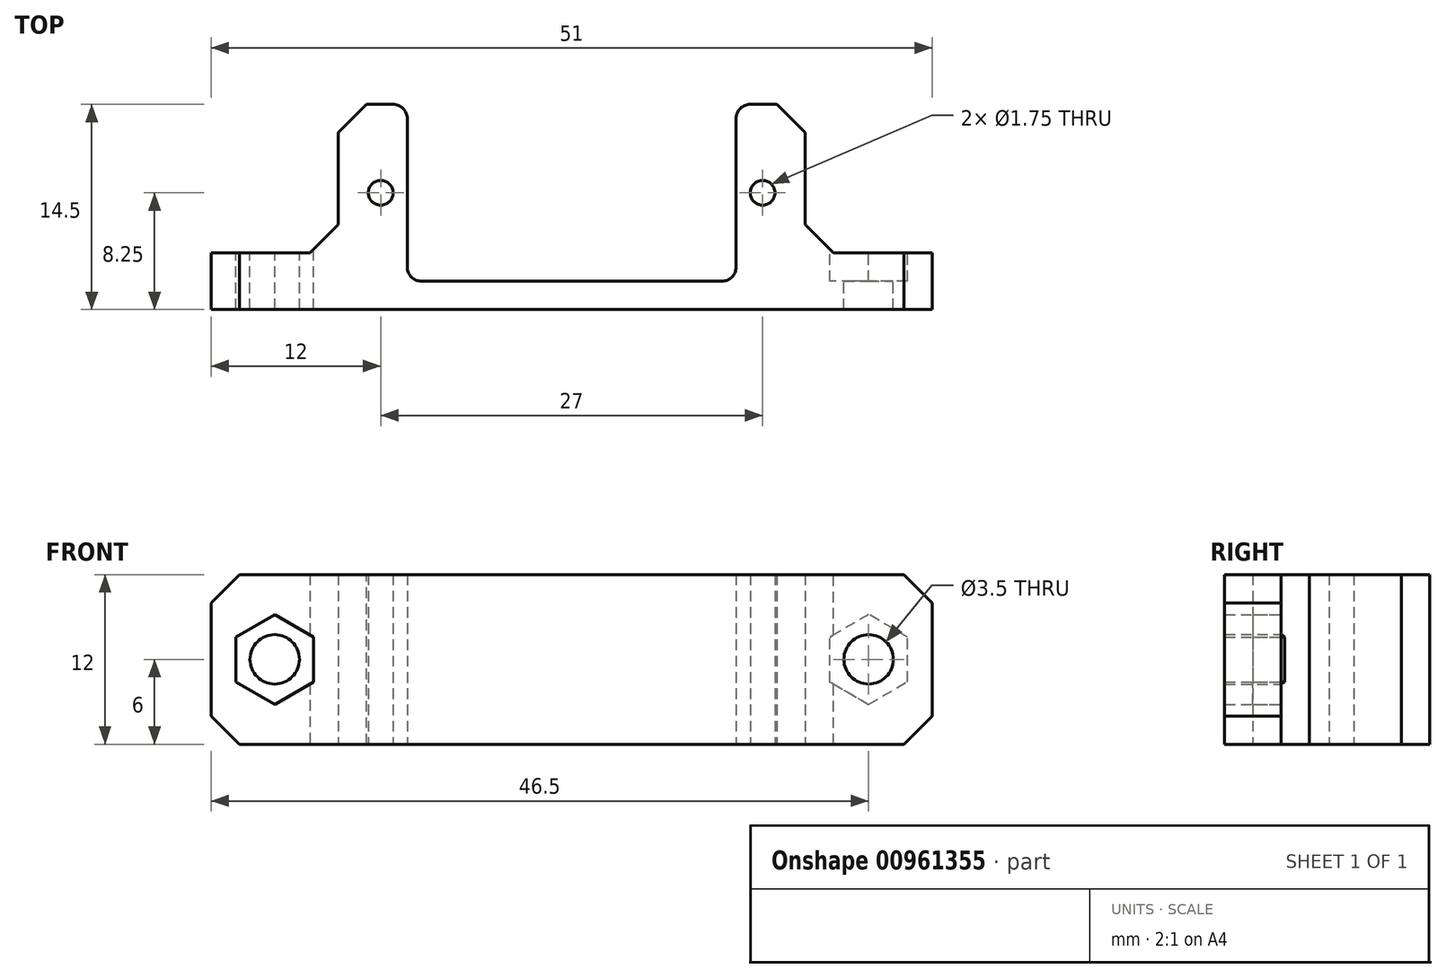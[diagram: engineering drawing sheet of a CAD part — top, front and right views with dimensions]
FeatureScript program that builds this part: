
annotation { "Feature Type Name" : "Feature", "Feature Type Description" : "" }
export const myFeature = defineFeature(function(context is Context, id is Id, definition is map)
    precondition{}
    {
        {
            var Q0;
            Q0=qCreatedBy(makeId("Top.planeOp"),FACE);
            var sketch = newSketch(context, id + "F0", { "sketchPlane" : qUnion([Q0])});
            skLineSegment(sketch, "E0.bottom", {"start": v(16.5, 7.25) * mm, "end": v(-16.5, 7.25) * mm});
            skLineSegment(sketch, "E0.top", {"start": v(16.5, -7.25) * mm, "end": v(-16.5, -7.25) * mm});
            skLineSegment(sketch, "E0.left", {"start": v(16.5, 7.25) * mm, "end": v(16.5, -7.25) * mm});
            skLineSegment(sketch, "E0.right", {"start": v(-16.5, 7.25) * mm, "end": v(-16.5, -7.25) * mm});
            skPoint(sketch, "E0.middle", {"position": v(0, 0) * mm});
            skLineSegment(sketch, "E1", {"start": v(-16.5, -5.25) * mm, "end": v(16.5, -5.25) * mm});
            skLineSegment(sketch, "E2", {"start": v(-11.62, 7.25) * mm, "end": v(-11.62, -5.25) * mm});
            skCircle(sketch, "E3", {"center": v(-13.5, 1) * mm, "radius": 0.88 * mm});
            skLineSegment(sketch, "E4.bottom", {"start": v(-25.5, -3.25) * mm, "end": v(-16.5, -3.25) * mm});
            skLineSegment(sketch, "E4.top", {"start": v(-25.5, -7.25) * mm, "end": v(-16.5, -7.25) * mm});
            skLineSegment(sketch, "E4.left", {"start": v(-25.5, -3.25) * mm, "end": v(-25.5, -7.25) * mm});
            skLineSegment(sketch, "E4.right", {"start": v(-16.5, -3.25) * mm, "end": v(-16.5, -7.25) * mm});
            skLineSegment(sketch, "E5.MirrorCS", {"start": v(11.62, 7.25) * mm, "end": v(11.62, -5.25) * mm});
            skCircle(sketch, "E6.MirrorC", {"center": v(13.5, 1) * mm, "radius": 0.88 * mm});
            skLineSegment(sketch, "E7.MirrorCS", {"start": v(25.5, -3.25) * mm, "end": v(16.5, -3.25) * mm});
            skLineSegment(sketch, "E8.MirrorCS", {"start": v(25.5, -3.25) * mm, "end": v(25.5, -7.25) * mm});
            skLineSegment(sketch, "E9.MirrorCS", {"start": v(25.5, -7.25) * mm, "end": v(16.5, -7.25) * mm});
            skSolve(sketch);
        }
        {
            var Q0;
            {var subQ4=sQuery(id+"F0.wireOp",EDGE,"E0.top");Q0=makeQuery(id+"F0.imprint","IMPRINT",FACE,{"disambiguationData":[TD([[makeQuery(id+"F0.imprint","IMPRINT",EDGE,{"derivedFrom":subQ4}),-1.0]])]});}
            var Q1;
            {var subQ4=sQuery(id+"F0.wireOp",EDGE,"E2");Q1=makeQuery(id+"F0.imprint","IMPRINT",FACE,{"disambiguationData":[TD([[makeQuery(id+"F0.imprint","IMPRINT",EDGE,{"derivedFrom":subQ4}),-1.0]])]});}
            var Q2;
            {var subQ6=sQuery(id+"F0.wireOp",EDGE,"E5.MirrorCS");Q2=makeQuery(id+"F0.imprint","IMPRINT",FACE,{"disambiguationData":[TD([[makeQuery(id+"F0.imprint","IMPRINT",EDGE,{"derivedFrom":subQ6}),1.0]])]});}
            var Q3;
            {var subQ3=sQuery(id+"F0.wireOp",EDGE,"E7.MirrorCS");Q3=makeQuery(id+"F0.imprint","IMPRINT",FACE,{"disambiguationData":[TD([[makeQuery(id+"F0.imprint","IMPRINT",EDGE,{"derivedFrom":subQ3}),1.0]])]});}
            var Q4;
            {var subQ1=sQuery(id+"F0.wireOp",EDGE,"E4.bottom");Q4=makeQuery(id+"F0.imprint","IMPRINT",FACE,{"disambiguationData":[TD([[makeQuery(id+"F0.imprint","IMPRINT",EDGE,{"derivedFrom":subQ1}),-1.0]])]});}
            extrude(context, id + "F1", {"entities" : qUnion([Q0, Q1, Q2, Q3, Q4]), "depth" : 12 * mm, "offsetDistance" : 25 * mm});
        }
        {
            var Q0;
            Q0=makeQuery(id+"F1.opExtrude","SWEPT_FACE",FACE,{"disambiguationData":[OSD([sQuery(id+"F0.wireOp",EDGE,"E7.MirrorCS")])]});
            var sketch = newSketch(context, id + "F2", { "sketchPlane" : qUnion([Q0])});
            skCircle(sketch, "E10.cCircle", {"center": v(-21, 6) * mm, "radius": 2.75 * mm, "construction": true});
            skLineSegment(sketch, "E10.0", {"start": v(-18.25, 7.59) * mm, "end": v(-18.25, 4.41) * mm});
            skLineSegment(sketch, "E10.1", {"start": v(-18.25, 4.41) * mm, "end": v(-21, 2.82) * mm});
            skLineSegment(sketch, "E10.2", {"start": v(-21, 2.82) * mm, "end": v(-23.75, 4.41) * mm});
            skLineSegment(sketch, "E10.3", {"start": v(-23.75, 4.41) * mm, "end": v(-23.75, 7.59) * mm});
            skLineSegment(sketch, "E10.4", {"start": v(-23.75, 7.59) * mm, "end": v(-21, 9.18) * mm});
            skLineSegment(sketch, "E10.5", {"start": v(-21, 9.18) * mm, "end": v(-18.25, 7.59) * mm});
            skPoint(sketch, "E10.0.midPoint", {"position": v(-18.25, 6) * mm});
            skCircle(sketch, "E11", {"center": v(-21, 6) * mm, "radius": 1.75 * mm});
            skLineSegment(sketch, "E12.MirrorCS", {"start": v(18.25, 7.59) * mm, "end": v(18.25, 4.41) * mm});
            skLineSegment(sketch, "E13.MirrorCS", {"start": v(21, 9.18) * mm, "end": v(18.25, 7.59) * mm});
            skLineSegment(sketch, "E14.MirrorCS", {"start": v(23.75, 7.59) * mm, "end": v(21, 9.18) * mm});
            skLineSegment(sketch, "E15.MirrorCS", {"start": v(23.75, 4.41) * mm, "end": v(23.75, 7.59) * mm});
            skLineSegment(sketch, "E16.MirrorCS", {"start": v(21, 2.82) * mm, "end": v(23.75, 4.41) * mm});
            skLineSegment(sketch, "E17.MirrorCS", {"start": v(18.25, 4.41) * mm, "end": v(21, 2.82) * mm});
            skCircle(sketch, "E18.MirrorC", {"center": v(21, 6) * mm, "radius": 1.75 * mm});
            skCircle(sketch, "E19.MirrorC", {"center": v(21, 6) * mm, "radius": 2.75 * mm, "construction": true});
            skPoint(sketch, "E20.MirrorP", {"position": v(18.25, 6) * mm});
            skSolve(sketch);
        }
        {
            var Q0;
            Q0=makeQuery(id+"F2.imprint","IMPRINT",FACE,{"disambiguationData":[TD([[makeQuery(id+"F2.imprint","IMPRINT",EDGE,{"derivedFrom":sQuery(id+"F2.wireOp",EDGE,"E11")}),1.0]])]});
            var Q1;
            Q1=makeQuery(id+"F2.imprint","IMPRINT",FACE,{"disambiguationData":[TD([[makeQuery(id+"F2.imprint","IMPRINT",EDGE,{"derivedFrom":sQuery(id+"F2.wireOp",EDGE,"E18.MirrorC")}),-1.0]])]});
            extrude(context, id + "F3", {"entities" : qUnion([Q0, Q1]), "operationType" : NewBodyOperationType.REMOVE, "endBound" : BoundingType.THROUGH_ALL, "oppositeDirection" : true, "depth" : 25 * mm, "offsetDistance" : 25 * mm});
        }
        {
            var Q0;
            Q0=makeQuery(id+"F2.imprint","IMPRINT",FACE,{"disambiguationData":[TD([[makeQuery(id+"F2.imprint","IMPRINT",EDGE,{"derivedFrom":sQuery(id+"F2.wireOp",EDGE,"E10.0")}),-1.0]])]});
            var Q1;
            Q1=makeQuery(id+"F2.imprint","IMPRINT",FACE,{"disambiguationData":[TD([[makeQuery(id+"F2.imprint","IMPRINT",EDGE,{"derivedFrom":sQuery(id+"F2.wireOp",EDGE,"E12.MirrorCS")}),1.0]])]});
            extrude(context, id + "F4", {"entities" : qUnion([Q0, Q1]), "operationType" : NewBodyOperationType.REMOVE, "oppositeDirection" : true, "depth" : 2 * mm, "offsetDistance" : 25 * mm});
        }
        {
            var Q0;
            Q0=makeQuery(id+"F1.opExtrude","SWEPT_EDGE",EDGE,{"disambiguationData":[OSD([sQuery(id+"F0.wireOp",EDGE,"E0.left"),sQuery(id+"F0.wireOp",EDGE,"E7.MirrorCS")])]});
            var Q1;
            Q1=makeQuery(id+"F1.opExtrude","CAP_EDGE",EDGE,{"disambiguationData":[OSD([sQuery(id+"F0.wireOp",EDGE,"E8.MirrorCS")])],"isStart":true});
            var Q2;
            Q2=makeQuery(id+"F1.opExtrude","CAP_EDGE",EDGE,{"disambiguationData":[OSD([sQuery(id+"F0.wireOp",EDGE,"E8.MirrorCS")])],"isStart":false});
            var Q3;
            Q3=makeQuery(id+"F1.opExtrude","SWEPT_EDGE",EDGE,{"disambiguationData":[OSD([sQuery(id+"F0.wireOp",EDGE,"E0.bottom"),sQuery(id+"F0.wireOp",EDGE,"E0.left")])]});
            var Q4;
            Q4=makeQuery(id+"F1.opExtrude","SWEPT_EDGE",EDGE,{"disambiguationData":[OSD([sQuery(id+"F0.wireOp",EDGE,"E0.bottom"),sQuery(id+"F0.wireOp",EDGE,"E0.right")])]});
            var Q5;
            Q5=makeQuery(id+"F1.opExtrude","SWEPT_EDGE",EDGE,{"disambiguationData":[OSD([sQuery(id+"F0.wireOp",EDGE,"E0.right"),sQuery(id+"F0.wireOp",EDGE,"E4.bottom")])]});
            var Q6;
            Q6=makeQuery(id+"F1.opExtrude","CAP_EDGE",EDGE,{"disambiguationData":[OSD([sQuery(id+"F0.wireOp",EDGE,"E4.left")])],"isStart":true});
            var Q7;
            Q7=makeQuery(id+"F1.opExtrude","CAP_EDGE",EDGE,{"disambiguationData":[OSD([sQuery(id+"F0.wireOp",EDGE,"E4.left")])],"isStart":false});
            chamfer(context, id + "F5", {"entities" : qUnion([Q0, Q1, Q2, Q3, Q4, Q5, Q6, Q7]), "width" : 2 * mm, "tangentPropagation" : true});
        }
        {
            var Q0;
            Q0=makeQuery(id+"F1.opExtrude","SWEPT_EDGE",EDGE,{"disambiguationData":[OSD([sQuery(id+"F0.wireOp",EDGE,"E0.bottom"),sQuery(id+"F0.wireOp",EDGE,"E2")])]});
            var Q1;
            Q1=makeQuery(id+"F1.opExtrude","SWEPT_EDGE",EDGE,{"disambiguationData":[OSD([sQuery(id+"F0.wireOp",EDGE,"E0.bottom"),sQuery(id+"F0.wireOp",EDGE,"E5.MirrorCS")])]});
            var Q2;
            Q2=makeQuery(id+"F1.opExtrude","SWEPT_EDGE",EDGE,{"disambiguationData":[OSD([sQuery(id+"F0.wireOp",EDGE,"E1"),sQuery(id+"F0.wireOp",EDGE,"E5.MirrorCS")])]});
            var Q3;
            Q3=makeQuery(id+"F1.opExtrude","SWEPT_EDGE",EDGE,{"disambiguationData":[OSD([sQuery(id+"F0.wireOp",EDGE,"E1"),sQuery(id+"F0.wireOp",EDGE,"E2")])]});
            fillet(context, id + "F6", {"entities" : qUnion([Q0, Q1, Q2, Q3]), "radius" : 1 * mm, "tangentPropagation" : true, "allowEdgeOverflow" : false});
        }
    });
